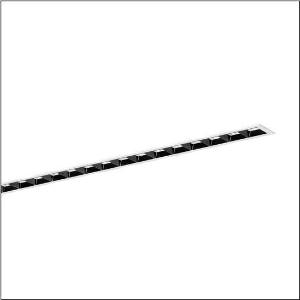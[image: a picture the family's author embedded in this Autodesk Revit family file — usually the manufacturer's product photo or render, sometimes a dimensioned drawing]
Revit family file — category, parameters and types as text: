
# Revit family: silica_r__21_51mx11da34wb_06c0
name_source: partatom
category: Lighting Fixtures
units: mm (PartAtom-declared; Revit-internal decimal feet)

## family parameters
Cut with Voids When Loaded = No
Host = Face
Light Source = No
Part Type = Normal
Room Calculation Point = No
Round Connector Dimension = Use Diameter
Shared = No

## types (1)
- --- (1 x LED, 4320 lm, 27.4 W, 3000K)
    Apparent Load = 27 VA
    CIE Flux Codes = 87 99 100 100 100
    Color Rendering = 80
    Color Temperature = 3000K
    Default Elevation = 1800 mm
    Description = Silica® 21, office luminaire, primary light control with darklight reflector, of PMMA, black, CAT 2 (L<= 3000cd/m²), light emission: direct distribution, primary light characteristic: symmetric, installation type: recessed, LED, rated luminous flux: 4.320lm, luminous efficacy: 158lm/W, light colour: 830, colour temperature: 3000K, with terminal, 3+2-pole, max. 2.5mm², mains connection: 220..240V, AC, 50/60Hz, rated input power: 27.4W, luminaire housing, of aluminium, traffic white (RAL 9016), length: 1.228mm, width: 79mm, height: 53mm, protection rating (complete): IP20, insulation class (complete): insulation class I (protective earthing), certification: CE, permissible operating ambient temperature: 0..+35°C, standard: EN 50419, packaging unit: 1 piece
    Height = 0 mm  [stored 0 ft]
    Lamp = 1 x LED
    Lamp Light Flux = 4320 lm
    Lamp Power = 27.4 W
    Lamp count = 1
    Length = 1227 mm
    Luminous efficacy = 158 lm/W
    Manufacturer = Siteco
    ModVariant = No
    Model = 51MX11DA34WB
    Mounting Place = Ceiling
    Mounting Type = Recessed
    Number of Poles = 1
    OnlyDefault = Yes
    Power Factor = 1
    Product Name = Silica® 21
    Product group = office luminaire | ceiling recessed
    ProductGroupID = 401
    Protection Class = Protection class I
    Protection Degree = IP 20
    RLX_Detail_Level = 1
    RLX_Emergency_Light_Flux = 0 lm
    RLX_Emergency_Type = 0
    RLX_Emergency_Type_DB = No
    RlxData = <blob elided: 39745 chars, md5=96f8e68f>
    Socket = socket
    Standby Power = 0 W
    System Light Flux = 4320 lm
    System Power = 27 W
    Type Comments = factory setting: luminous flux: 100 % | dim-lin: 254 | 393 mA
    Type Image = l_1297791.jpg
    URL = http://relux.com
    VarID = @adj_054191
    Voltage = 0 V
    Weight = 0.00 kg
    Width = 79 mm

note: [stored X ft] marks values corroborated as IEEE doubles in the binary element streams (Revit-internal decimal feet)

## geometry (parser evidence)
native form markers: Blend x4, Sweep x10
no freeform markers — native parametric forms only
